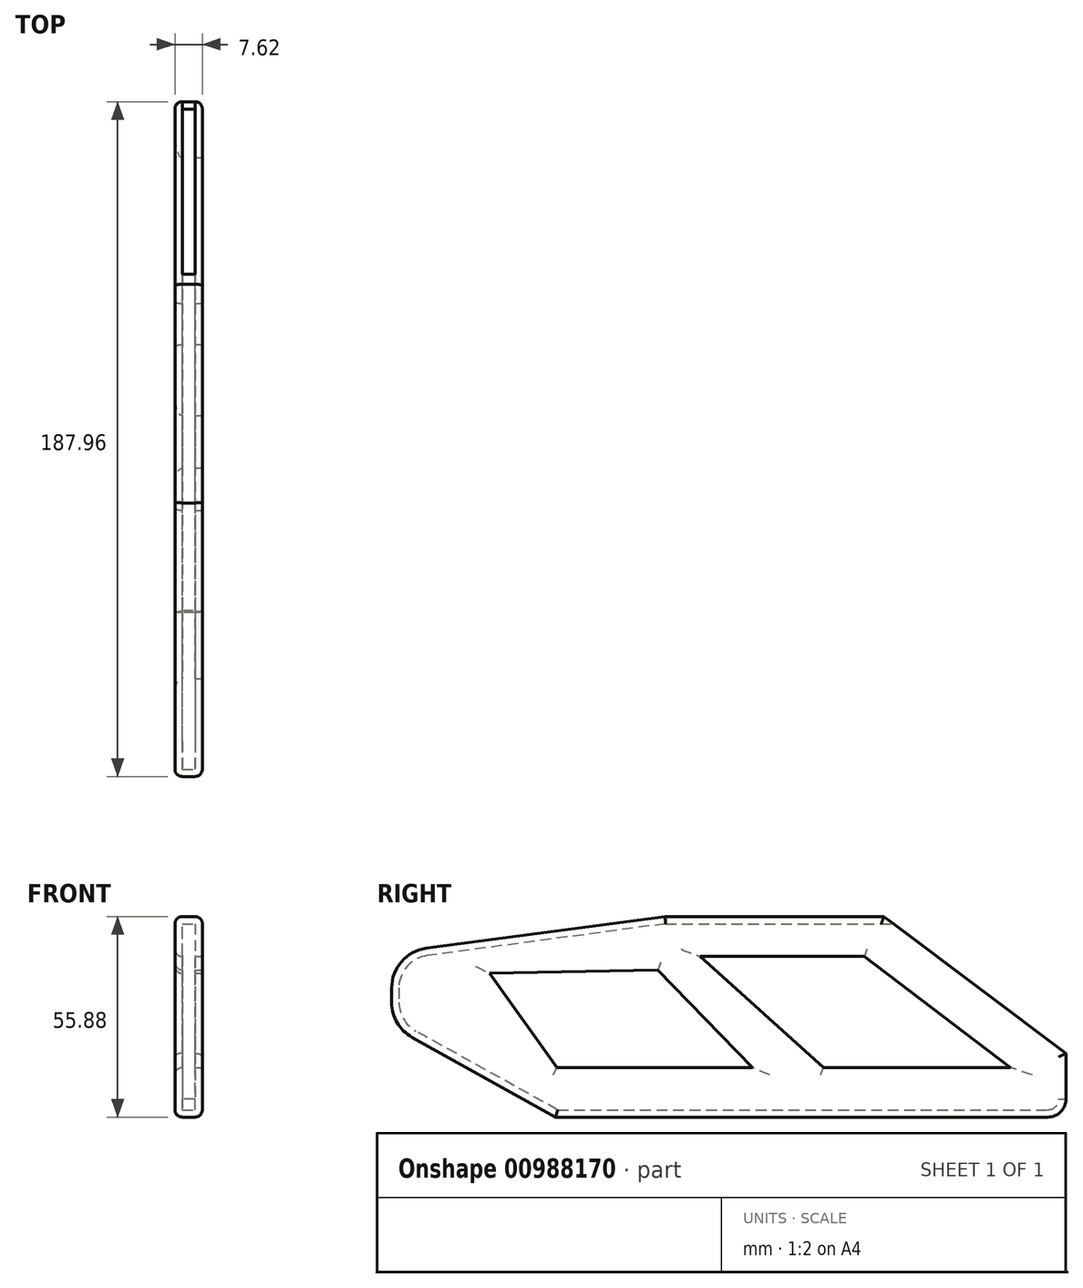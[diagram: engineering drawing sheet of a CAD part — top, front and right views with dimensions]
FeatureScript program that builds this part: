
annotation { "Feature Type Name" : "Feature", "Feature Type Description" : "" }
export const myFeature = defineFeature(function(context is Context, id is Id, definition is map)
    precondition{}
    {
        {
            var Q0;
            Q0=qCreatedBy(makeId("Right.planeOp"),FACE);
            var sketch = newSketch(context, id + "F0", { "sketchPlane" : qUnion([Q0])});
            skLineSegment(sketch, "E0.bottom", {"start": v(-74.15, 30.28) * mm, "end": v(113.81, 30.28) * mm});
            skLineSegment(sketch, "E0.top", {"start": v(-74.15, -25.6) * mm, "end": v(113.81, -25.6) * mm});
            skLineSegment(sketch, "E0.left", {"start": v(-74.15, 30.28) * mm, "end": v(-74.15, -25.6) * mm});
            skLineSegment(sketch, "E0.right", {"start": v(113.81, 30.28) * mm, "end": v(113.81, -25.6) * mm});
            skSolve(sketch);
        }
        {
            var Q0;
            Q0=makeQuery(id+"F0.imprint","IMPRINT",FACE,{"disambiguationData":[TD([[makeQuery(id+"F0.imprint","IMPRINT",EDGE,{"derivedFrom":sQuery(id+"F0.wireOp",EDGE,"E0.bottom")}),-1.0]])]});
            extrude(context, id + "F1", {"entities" : qUnion([Q0]), "depth" : 7.62 * mm, "offsetDistance" : 25.4 * mm});
        }
        {
            var Q0;
            Q0=makeQuery(id+"F1.opExtrude","SWEPT_EDGE",EDGE,{"disambiguationData":[OSD([sQuery(id+"F0.wireOp",EDGE,"E0.bottom"),sQuery(id+"F0.wireOp",EDGE,"E0.right")])]});
            chamfer(context, id + "F2", {"entities" : qUnion([Q0]), "chamferType" : ChamferType.TWO_OFFSETS, "width1" : 50.8 * mm, "oppositeDirection" : false, "width2" : 38.1 * mm});
        }
        {
            var Q0;
            Q0=makeQuery(id+"F1.opExtrude","SWEPT_EDGE",EDGE,{"disambiguationData":[OSD([sQuery(id+"F0.wireOp",EDGE,"E0.top"),sQuery(id+"F0.wireOp",EDGE,"E0.left")])]});
            chamfer(context, id + "F3", {"entities" : qUnion([Q0]), "chamferType" : ChamferType.TWO_OFFSETS, "width1" : 45.72 * mm, "oppositeDirection" : false, "width2" : 25.4 * mm, "tangentPropagation" : true});
        }
        {
            var Q0;
            Q0=makeQuery(id+"F1.opExtrude","SWEPT_EDGE",EDGE,{"disambiguationData":[OSD([sQuery(id+"F0.wireOp",EDGE,"E0.bottom"),sQuery(id+"F0.wireOp",EDGE,"E0.left")])]});
            chamfer(context, id + "F4", {"entities" : qUnion([Q0]), "chamferType" : ChamferType.TWO_OFFSETS, "width1" : 10.16 * mm, "oppositeDirection" : false, "width2" : 76.2 * mm});
        }
        {
            var Q0;
            Q0=makeQuery(id+"F1.opExtrude","SWEPT_EDGE",EDGE,{"disambiguationData":[OSD([sQuery(id+"F0.wireOp",EDGE,"E0.top"),sQuery(id+"F0.wireOp",EDGE,"E0.right")])]});
            fillet(context, id + "F5", {"entities" : qUnion([Q0]), "radius" : 5.08 * mm, "tangentPropagation" : true, "allowEdgeOverflow" : false});
        }
        {
            var Q0;
            {var subQ0=sQuery(id+"F0.wireOp",EDGE,"E0.left");Q0=makeQuery(id+"F4.opChamfer","BLEND_EDGE",EDGE,{"blendedFrom":[makeQuery(id+"F1.opExtrude","SWEPT_EDGE",EDGE,{"disambiguationData":[OSD([sQuery(id+"F0.wireOp",EDGE,"E0.bottom"),subQ0])]}),makeQuery(id+"F1.opExtrude","SWEPT_FACE",FACE,{"disambiguationData":[OSD([subQ0])]})],"blendedInto":[makeQuery(id+"F1.opExtrude","SWEPT_FACE",FACE,{"disambiguationData":[OSD([subQ0])]})]});}
            var Q1;
            {var subQ0=sQuery(id+"F0.wireOp",EDGE,"E0.left");Q1=makeQuery(id+"F3.opChamfer","BLEND_EDGE",EDGE,{"blendedFrom":[makeQuery(id+"F1.opExtrude","SWEPT_EDGE",EDGE,{"disambiguationData":[OSD([sQuery(id+"F0.wireOp",EDGE,"E0.top"),subQ0])]}),makeQuery(id+"F1.opExtrude","SWEPT_FACE",FACE,{"disambiguationData":[OSD([subQ0])]})],"blendedInto":[makeQuery(id+"F1.opExtrude","SWEPT_FACE",FACE,{"disambiguationData":[OSD([subQ0])]})]});}
            fillet(context, id + "F6", {"entities" : qUnion([Q0, Q1]), "radius" : 11.1 * mm, "tangentPropagation" : true, "allowEdgeOverflow" : false});
        }
        {
            var Q0;
            Q0=makeQuery(id+"F2.opChamfer","BLEND_FACE",FACE,{"disambiguationData":[OSD([sQuery(id+"F0.wireOp",EDGE,"E0.bottom"),sQuery(id+"F0.wireOp",EDGE,"E0.right")])]});
            var Q1;
            Q1=makeQuery(id+"F1.opExtrude","SWEPT_FACE",FACE,{"disambiguationData":[OSD([sQuery(id+"F0.wireOp",EDGE,"E0.right")])]});
            shell(context, id + "F7", {"entities" : qUnion([Q0, Q1]), "thickness" : 2.03 * mm});
        }
        {
            var Q0;
            Q0=makeQuery(id+"F1.opExtrude","CAP_FACE",FACE,{"disambiguationData":[OSD([sQuery(id+"F0.wireOp",EDGE,"E0.bottom"),sQuery(id+"F0.wireOp",EDGE,"E0.top"),sQuery(id+"F0.wireOp",EDGE,"E0.left"),sQuery(id+"F0.wireOp",EDGE,"E0.right")])],"isStart":false});
            var sketch = newSketch(context, id + "F8", { "sketchPlane" : qUnion([Q0])});
            skLineSegment(sketch, "E1", {"start": v(-46.85, 14.45) * mm, "end": v(0, 15.43) * mm});
            skLineSegment(sketch, "E2", {"start": v(0, 15.43) * mm, "end": v(26.41, -11.79) * mm});
            skLineSegment(sketch, "E3", {"start": v(26.41, -11.79) * mm, "end": v(-28.09, -11.79) * mm});
            skLineSegment(sketch, "E4", {"start": v(-28.09, -11.79) * mm, "end": v(-46.85, 14.45) * mm});
            skLineSegment(sketch, "E5", {"start": v(11.77, 19.14) * mm, "end": v(46.16, -11.79) * mm});
            skLineSegment(sketch, "E6", {"start": v(46.16, -11.79) * mm, "end": v(98.32, -11.79) * mm});
            skLineSegment(sketch, "E7", {"start": v(98.32, -11.79) * mm, "end": v(57.59, 19.14) * mm});
            skLineSegment(sketch, "E8", {"start": v(57.59, 19.14) * mm, "end": v(11.77, 19.14) * mm});
            skSolve(sketch);
        }
        {
            var Q0;
            Q0=makeQuery(id+"F8.imprint","IMPRINT",FACE,{"disambiguationData":[TD([[makeQuery(id+"F8.imprint","IMPRINT",EDGE,{"derivedFrom":sQuery(id+"F8.wireOp",EDGE,"E1")}),-1.0]])]});
            var Q1;
            Q1=makeQuery(id+"F8.imprint","IMPRINT",FACE,{"disambiguationData":[TD([[makeQuery(id+"F8.imprint","IMPRINT",EDGE,{"derivedFrom":sQuery(id+"F8.wireOp",EDGE,"E5")}),1.0]])]});
            extrude(context, id + "F9", {"entities" : qUnion([Q0, Q1]), "operationType" : NewBodyOperationType.REMOVE, "oppositeDirection" : true, "depth" : 64.77 * mm, "offsetDistance" : 25.4 * mm});
        }
        {
            var Q0;
            {var subQ0=sQuery(id+"F0.wireOp",EDGE,"E0.left");var subQ1=sQuery(id+"F0.wireOp",EDGE,"E0.bottom");Q0=makeQuery(id+"F4.opChamfer","BLEND_EDGE",EDGE,{"blendedFrom":[makeQuery(id+"F1.opExtrude","SWEPT_EDGE",EDGE,{"disambiguationData":[OSD([subQ1,subQ0])]}),makeQuery(id+"F1.opExtrude","CAP_FACE",FACE,{"disambiguationData":[OSD([subQ1,sQuery(id+"F0.wireOp",EDGE,"E0.top"),subQ0,sQuery(id+"F0.wireOp",EDGE,"E0.right")])],"isStart":false})],"blendedInto":[makeQuery(id+"F1.opExtrude","CAP_FACE",FACE,{"disambiguationData":[OSD([subQ1,sQuery(id+"F0.wireOp",EDGE,"E0.top"),subQ0,sQuery(id+"F0.wireOp",EDGE,"E0.right")])],"isStart":false})]});}
            var Q1;
            Q1=makeQuery(id+"F1.opExtrude","CAP_EDGE",EDGE,{"disambiguationData":[OSD([sQuery(id+"F0.wireOp",EDGE,"E0.bottom")])],"isStart":false});
            var Q2;
            {var subQ0=sQuery(id+"F0.wireOp",EDGE,"E0.left");var subQ1=sQuery(id+"F0.wireOp",EDGE,"E0.bottom");Q2=makeQuery(id+"F4.opChamfer","BLEND_EDGE",EDGE,{"blendedFrom":[makeQuery(id+"F1.opExtrude","SWEPT_EDGE",EDGE,{"disambiguationData":[OSD([subQ1,subQ0])]}),makeQuery(id+"F1.opExtrude","CAP_FACE",FACE,{"disambiguationData":[OSD([subQ1,sQuery(id+"F0.wireOp",EDGE,"E0.top"),subQ0,sQuery(id+"F0.wireOp",EDGE,"E0.right")])],"isStart":true})],"blendedInto":[makeQuery(id+"F1.opExtrude","CAP_FACE",FACE,{"disambiguationData":[OSD([subQ1,sQuery(id+"F0.wireOp",EDGE,"E0.top"),subQ0,sQuery(id+"F0.wireOp",EDGE,"E0.right")])],"isStart":true})]});}
            var Q3;
            Q3=makeQuery(id+"F1.opExtrude","CAP_EDGE",EDGE,{"disambiguationData":[OSD([sQuery(id+"F0.wireOp",EDGE,"E0.bottom")])],"isStart":true});
            var Q4;
            Q4=makeQuery(id+"F1.opExtrude","CAP_EDGE",EDGE,{"disambiguationData":[OSD([sQuery(id+"F0.wireOp",EDGE,"E0.top")])],"isStart":true});
            var Q5;
            Q5=makeQuery(id+"F1.opExtrude","CAP_EDGE",EDGE,{"disambiguationData":[OSD([sQuery(id+"F0.wireOp",EDGE,"E0.top")])],"isStart":false});
            var Q6;
            {var subQ0=sQuery(id+"F0.wireOp",EDGE,"E0.right");var subQ1=sQuery(id+"F0.wireOp",EDGE,"E0.bottom");Q6=makeQuery(id+"F2.opChamfer","BLEND_EDGE",EDGE,{"blendedFrom":[makeQuery(id+"F1.opExtrude","SWEPT_EDGE",EDGE,{"disambiguationData":[OSD([subQ1,subQ0])]}),makeQuery(id+"F1.opExtrude","CAP_FACE",FACE,{"disambiguationData":[OSD([subQ1,sQuery(id+"F0.wireOp",EDGE,"E0.top"),sQuery(id+"F0.wireOp",EDGE,"E0.left"),subQ0])],"isStart":false})],"blendedInto":[makeQuery(id+"F1.opExtrude","CAP_FACE",FACE,{"disambiguationData":[OSD([subQ1,sQuery(id+"F0.wireOp",EDGE,"E0.top"),sQuery(id+"F0.wireOp",EDGE,"E0.left"),subQ0])],"isStart":false})]});}
            var Q7;
            Q7=makeQuery(id+"F9.boolean.opBoolean","COPY",EDGE,{"derivedFrom":makeQuery(id+"F9.opExtrude","CAP_EDGE",EDGE,{"disambiguationData":[OSD([sQuery(id+"F8.wireOp",EDGE,"E1")])],"isStart":true})});
            var Q8;
            Q8=makeQuery(id+"F9.boolean.opBoolean","COPY",EDGE,{"derivedFrom":makeQuery(id+"F9.opExtrude","CAP_EDGE",EDGE,{"disambiguationData":[OSD([sQuery(id+"F8.wireOp",EDGE,"E2")])],"isStart":true})});
            var Q9;
            Q9=makeQuery(id+"F9.boolean.opBoolean","COPY",EDGE,{"derivedFrom":makeQuery(id+"F9.opExtrude","CAP_EDGE",EDGE,{"disambiguationData":[OSD([sQuery(id+"F8.wireOp",EDGE,"E5")])],"isStart":true})});
            var Q10;
            Q10=makeQuery(id+"F9.boolean.opBoolean","COPY",EDGE,{"derivedFrom":makeQuery(id+"F9.opExtrude","CAP_EDGE",EDGE,{"disambiguationData":[OSD([sQuery(id+"F8.wireOp",EDGE,"E4")])],"isStart":true})});
            var Q11;
            Q11=makeQuery(id+"F9.boolean.opBoolean","INTERSECT",EDGE,{"derivedFrom":[makeQuery(id+"F1.opExtrude","CAP_FACE",FACE,{"disambiguationData":[OSD([sQuery(id+"F0.wireOp",EDGE,"E0.bottom"),sQuery(id+"F0.wireOp",EDGE,"E0.top"),sQuery(id+"F0.wireOp",EDGE,"E0.left"),sQuery(id+"F0.wireOp",EDGE,"E0.right")])],"isStart":true}),makeQuery(id+"F9.opExtrude","SWEPT_FACE",FACE,{"disambiguationData":[OSD([sQuery(id+"F8.wireOp",EDGE,"E4")])]})]});
            var Q12;
            Q12=makeQuery(id+"F9.boolean.opBoolean","INTERSECT",EDGE,{"derivedFrom":[makeQuery(id+"F1.opExtrude","CAP_FACE",FACE,{"disambiguationData":[OSD([sQuery(id+"F0.wireOp",EDGE,"E0.bottom"),sQuery(id+"F0.wireOp",EDGE,"E0.top"),sQuery(id+"F0.wireOp",EDGE,"E0.left"),sQuery(id+"F0.wireOp",EDGE,"E0.right")])],"isStart":true}),makeQuery(id+"F9.opExtrude","SWEPT_FACE",FACE,{"disambiguationData":[OSD([sQuery(id+"F8.wireOp",EDGE,"E3")])]})]});
            var Q13;
            Q13=makeQuery(id+"F9.boolean.opBoolean","INTERSECT",EDGE,{"derivedFrom":[makeQuery(id+"F1.opExtrude","CAP_FACE",FACE,{"disambiguationData":[OSD([sQuery(id+"F0.wireOp",EDGE,"E0.bottom"),sQuery(id+"F0.wireOp",EDGE,"E0.top"),sQuery(id+"F0.wireOp",EDGE,"E0.left"),sQuery(id+"F0.wireOp",EDGE,"E0.right")])],"isStart":true}),makeQuery(id+"F9.opExtrude","SWEPT_FACE",FACE,{"disambiguationData":[OSD([sQuery(id+"F8.wireOp",EDGE,"E2")])]})]});
            var Q14;
            Q14=makeQuery(id+"F9.boolean.opBoolean","INTERSECT",EDGE,{"derivedFrom":[makeQuery(id+"F1.opExtrude","CAP_FACE",FACE,{"disambiguationData":[OSD([sQuery(id+"F0.wireOp",EDGE,"E0.bottom"),sQuery(id+"F0.wireOp",EDGE,"E0.top"),sQuery(id+"F0.wireOp",EDGE,"E0.left"),sQuery(id+"F0.wireOp",EDGE,"E0.right")])],"isStart":true}),makeQuery(id+"F9.opExtrude","SWEPT_FACE",FACE,{"disambiguationData":[OSD([sQuery(id+"F8.wireOp",EDGE,"E1")])]})]});
            var Q15;
            Q15=makeQuery(id+"F9.boolean.opBoolean","INTERSECT",EDGE,{"derivedFrom":[makeQuery(id+"F1.opExtrude","CAP_FACE",FACE,{"disambiguationData":[OSD([sQuery(id+"F0.wireOp",EDGE,"E0.bottom"),sQuery(id+"F0.wireOp",EDGE,"E0.top"),sQuery(id+"F0.wireOp",EDGE,"E0.left"),sQuery(id+"F0.wireOp",EDGE,"E0.right")])],"isStart":true}),makeQuery(id+"F9.opExtrude","SWEPT_FACE",FACE,{"disambiguationData":[OSD([sQuery(id+"F8.wireOp",EDGE,"E5")])]})]});
            var Q16;
            Q16=makeQuery(id+"F9.boolean.opBoolean","INTERSECT",EDGE,{"derivedFrom":[makeQuery(id+"F1.opExtrude","CAP_FACE",FACE,{"disambiguationData":[OSD([sQuery(id+"F0.wireOp",EDGE,"E0.bottom"),sQuery(id+"F0.wireOp",EDGE,"E0.top"),sQuery(id+"F0.wireOp",EDGE,"E0.left"),sQuery(id+"F0.wireOp",EDGE,"E0.right")])],"isStart":true}),makeQuery(id+"F9.opExtrude","SWEPT_FACE",FACE,{"disambiguationData":[OSD([sQuery(id+"F8.wireOp",EDGE,"E8")])]})]});
            var Q17;
            Q17=makeQuery(id+"F1.opExtrude","CAP_FACE",FACE,{"disambiguationData":[OSD([sQuery(id+"F0.wireOp",EDGE,"E0.bottom"),sQuery(id+"F0.wireOp",EDGE,"E0.top"),sQuery(id+"F0.wireOp",EDGE,"E0.left"),sQuery(id+"F0.wireOp",EDGE,"E0.right")])],"isStart":true});
            var Q18;
            Q18=makeQuery(id+"F9.boolean.opBoolean","COPY",EDGE,{"derivedFrom":makeQuery(id+"F9.opExtrude","CAP_EDGE",EDGE,{"disambiguationData":[OSD([sQuery(id+"F8.wireOp",EDGE,"E6")])],"isStart":true})});
            var Q19;
            Q19=makeQuery(id+"F9.boolean.opBoolean","COPY",EDGE,{"derivedFrom":makeQuery(id+"F9.opExtrude","CAP_EDGE",EDGE,{"disambiguationData":[OSD([sQuery(id+"F8.wireOp",EDGE,"E3")])],"isStart":true})});
            var Q20;
            Q20=makeQuery(id+"F9.boolean.opBoolean","COPY",EDGE,{"derivedFrom":makeQuery(id+"F9.opExtrude","CAP_EDGE",EDGE,{"disambiguationData":[OSD([sQuery(id+"F8.wireOp",EDGE,"E7")])],"isStart":true})});
            var Q21;
            Q21=makeQuery(id+"F9.boolean.opBoolean","COPY",EDGE,{"derivedFrom":makeQuery(id+"F9.opExtrude","CAP_EDGE",EDGE,{"disambiguationData":[OSD([sQuery(id+"F8.wireOp",EDGE,"E8")])],"isStart":true})});
            fillet(context, id + "F10", {"entities" : qUnion([Q0, Q1, Q2, Q3, Q4, Q5, Q6, Q7, Q8, Q9, Q10, Q11, Q12, Q13, Q14, Q15, Q16, Q17, Q18, Q19, Q20, Q21]), "radius" : 2.03 * mm, "tangentPropagation" : true, "allowEdgeOverflow" : false});
        }
    });
